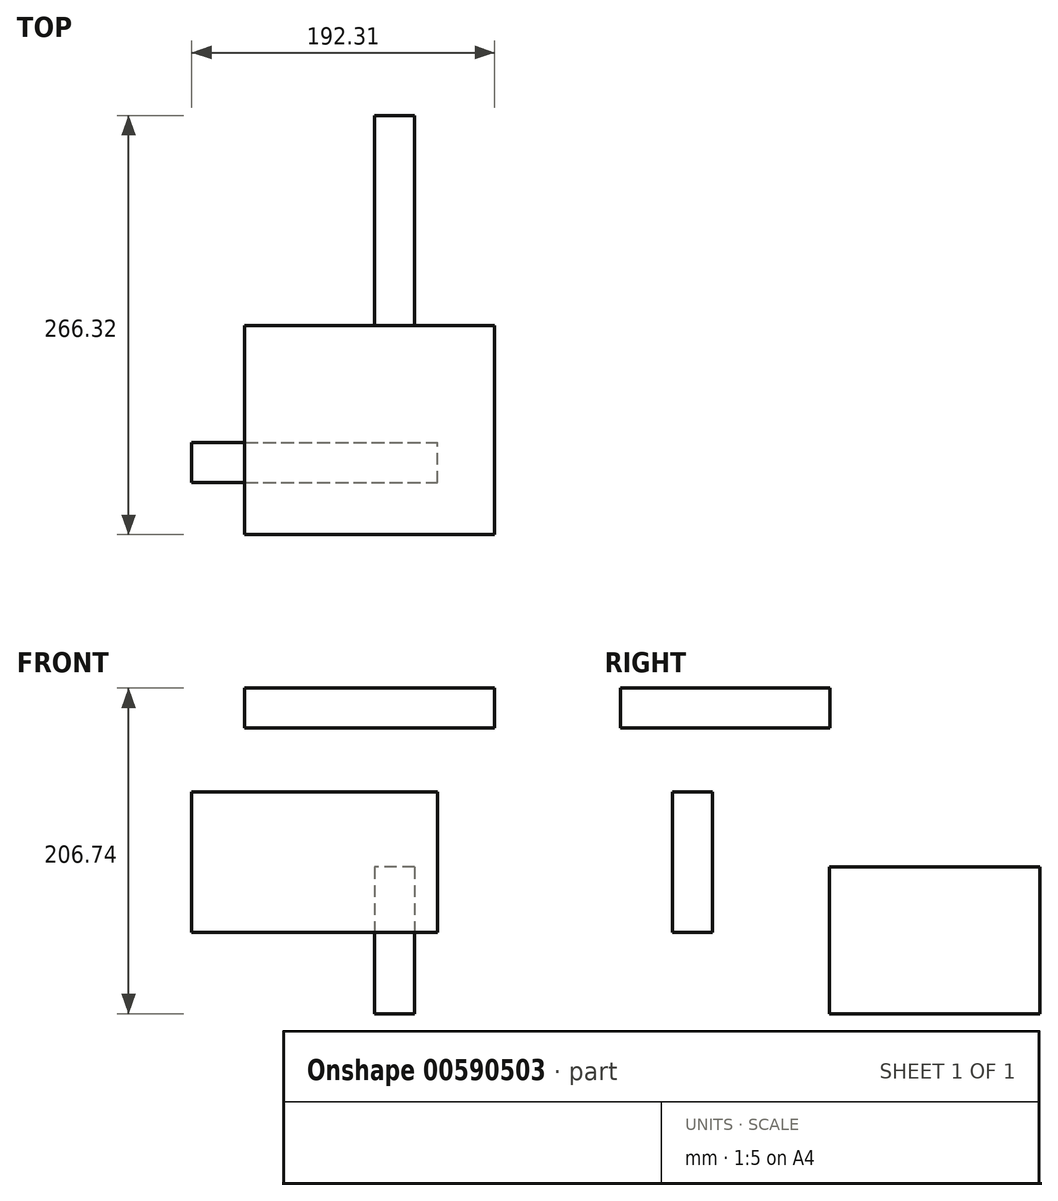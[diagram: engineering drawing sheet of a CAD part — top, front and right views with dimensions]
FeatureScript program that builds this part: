
annotation { "Feature Type Name" : "Feature", "Feature Type Description" : "" }
export const myFeature = defineFeature(function(context is Context, id is Id, definition is map)
    precondition{}
    {
        {
            var Q0;
            Q0=qCreatedBy(makeId("Top.planeOp"),FACE);
            var sketch = newSketch(context, id + "F0", { "sketchPlane" : qUnion([Q0])});
            skLineSegment(sketch, "E0.bottom", {"start": v(-82.46, -58.39) * mm, "end": v(76.14, -58.39) * mm});
            skLineSegment(sketch, "E0.top", {"start": v(-82.46, 74.56) * mm, "end": v(76.14, 74.56) * mm});
            skLineSegment(sketch, "E0.left", {"start": v(-82.46, -58.39) * mm, "end": v(-82.46, 74.56) * mm});
            skLineSegment(sketch, "E0.right", {"start": v(76.14, -58.39) * mm, "end": v(76.14, 74.56) * mm});
            skSolve(sketch);
        }
        {
            var Q0;
            Q0 = qSketchRegion(id + "F0", true);
            extrude(context, id + "F1", {"entities" : qUnion([Q0]), "depth" : 25.4 * mm, "offsetDistance" : 25.4 * mm});
        }
        {
            var Q0;
            Q0=qCreatedBy(makeId("Right.planeOp"),FACE);
            var sketch = newSketch(context, id + "F2", { "sketchPlane" : qUnion([Q0])});
            skLineSegment(sketch, "E1.bottom", {"start": v(74.29, -88.22) * mm, "end": v(207.93, -88.22) * mm});
            skLineSegment(sketch, "E1.top", {"start": v(74.29, -181.34) * mm, "end": v(207.93, -181.34) * mm});
            skLineSegment(sketch, "E1.left", {"start": v(74.29, -88.22) * mm, "end": v(74.29, -181.34) * mm});
            skLineSegment(sketch, "E1.right", {"start": v(207.93, -88.22) * mm, "end": v(207.93, -181.34) * mm});
            skSolve(sketch);
        }
        {
            var Q0;
            Q0 = qSketchRegion(id + "F2", true);
            extrude(context, id + "F3", {"entities" : qUnion([Q0]), "depth" : 25.4 * mm, "offsetDistance" : 25.4 * mm});
        }
        {
            var Q0;
            Q0=qCreatedBy(makeId("Front.planeOp"),FACE);
            var sketch = newSketch(context, id + "F4", { "sketchPlane" : qUnion([Q0])});
            skLineSegment(sketch, "E2.bottom", {"start": v(-116.17, -40.65) * mm, "end": v(39.87, -40.65) * mm});
            skLineSegment(sketch, "E2.top", {"start": v(-116.17, -129.66) * mm, "end": v(39.87, -129.66) * mm});
            skLineSegment(sketch, "E2.left", {"start": v(-116.17, -40.65) * mm, "end": v(-116.17, -129.66) * mm});
            skLineSegment(sketch, "E2.right", {"start": v(39.87, -40.65) * mm, "end": v(39.87, -129.66) * mm});
            skSolve(sketch);
        }
        {
            var Q0;
            Q0 = qSketchRegion(id + "F4", true);
            extrude(context, id + "F5", {"entities" : qUnion([Q0]), "depth" : 25.4 * mm, "offsetDistance" : 25.4 * mm});
        }
    });
